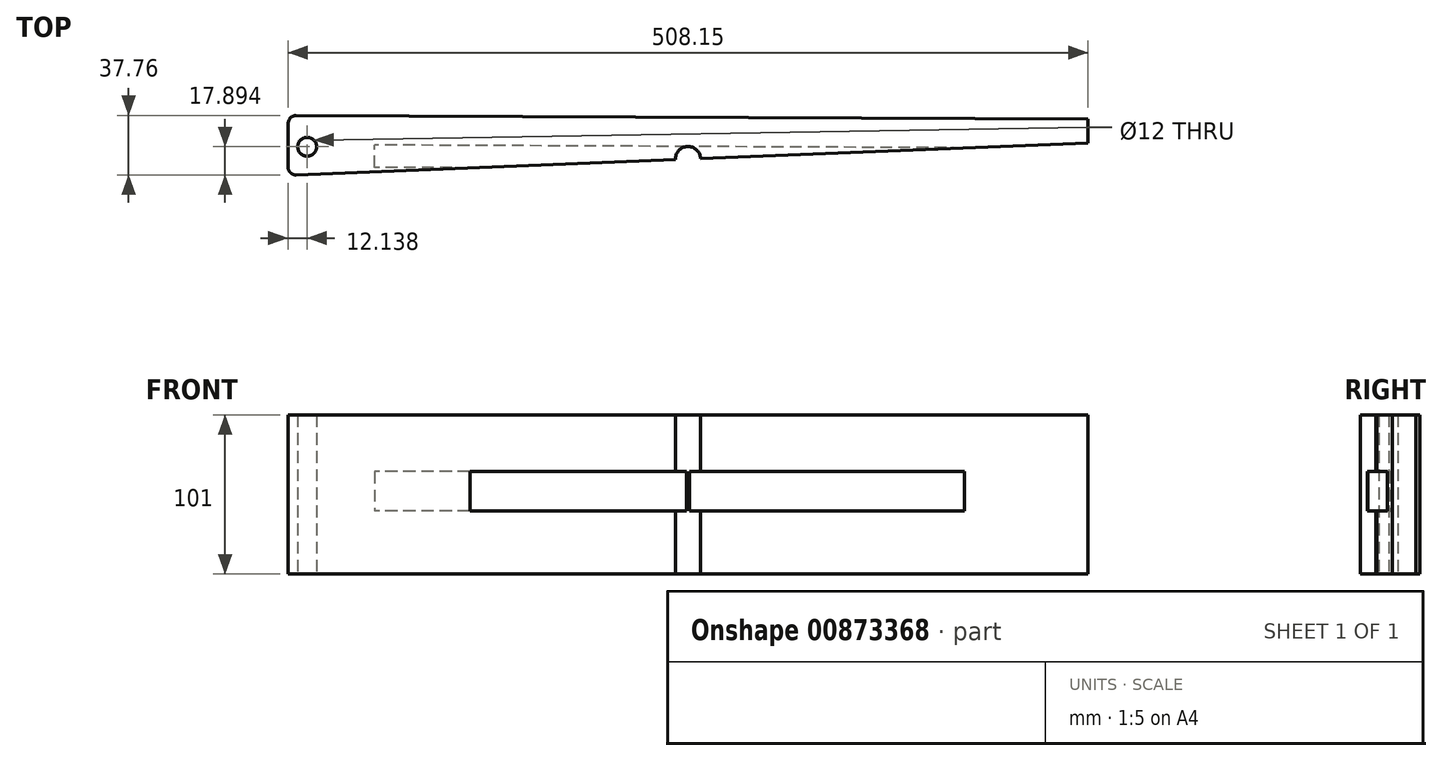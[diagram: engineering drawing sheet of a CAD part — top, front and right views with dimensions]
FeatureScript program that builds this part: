
annotation { "Feature Type Name" : "Feature", "Feature Type Description" : "" }
export const myFeature = defineFeature(function(context is Context, id is Id, definition is map)
    precondition{}
    {
        {
            var Q0;
            Q0=qCreatedBy(makeId("Top.planeOp"),FACE);
            var sketch = newSketch(context, id + "F0", { "sketchPlane" : qUnion([Q0])});
            skLineSegment(sketch, "E0.left", {"start": v(-253.96, 8.7) * mm, "end": v(-254.14, -29.3) * mm});
            skLineSegment(sketch, "E0.right", {"start": v(254.03, 6.3) * mm, "end": v(253.96, -8.7) * mm});
            skPoint(sketch, "E0.middle", {"position": v(0, 0) * mm});
            skLineSegment(sketch, "E1", {"start": v(-253.96, 8.7) * mm, "end": v(254.03, 6.3) * mm});
            skLineSegment(sketch, "E2", {"start": v(-254.14, -29.3) * mm, "end": v(253.96, -8.7) * mm});
            skCircle(sketch, "E3", {"center": v(-241.98, -11.19) * mm, "radius": 6 * mm});
            skPoint(sketch, "E3.centerSnap0", {"position": v(-254.14, -16.57) * mm});
            skCircle(sketch, "E4", {"center": v(-0.1, -19) * mm, "radius": 5 * mm});
            skCircle(sketch, "E5", {"center": v(-0.1, -19) * mm, "radius": 8 * mm});
            skLineSegment(sketch, "E6", {"start": v(-8.08, -19.32) * mm, "end": v(-5.09, -19.2) * mm});
            skLineSegment(sketch, "E7", {"start": v(4.9, -18.8) * mm, "end": v(7.9, -18.68) * mm});
            skSolve(sketch);
        }
        {
            var Q0;
            {var subQ1=sQuery(id+"F0.wireOp",EDGE,"E0.left");Q0=makeQuery(id+"F0.imprint","IMPRINT",FACE,{"disambiguationData":[TD([[makeQuery(id+"F0.imprint","IMPRINT",EDGE,{"derivedFrom":subQ1}),1.0]])]});}
            var Q1;
            {var subQ0=sQuery(id+"F0.wireOp",EDGE,"XZyqKKFk-1wkg-4Na5-50VD-DDx1DZDhWvUQ");Q1=makeQuery(id+"F0.imprint","IMPRINT",FACE,{"disambiguationData":[TD([[makeQuery(id+"F0.imprint","IMPRINT",EDGE,{"derivedFrom":subQ0}),1.0]])]});}
            var Q2;
            {var subQ5=sQuery(id+"F0.wireOp",EDGE,"XZyqKKFk-1wkg-4Na5-50VD-DDx1DZDhWvUQ");Q2=makeQuery(id+"F0.imprint","IMPRINT",FACE,{"disambiguationData":[TD([[makeQuery(id+"F0.imprint","IMPRINT",EDGE,{"derivedFrom":subQ5}),-1.0]])]});}
            var Q3;
            {var subQ5=sQuery(id+"F0.wireOp",EDGE,"MujNKNQA-XHeN-e8O0-YI1s-Rprdn2XYs7TK");Q3=makeQuery(id+"F0.imprint","IMPRINT",FACE,{"disambiguationData":[TD([[makeQuery(id+"F0.imprint","IMPRINT",EDGE,{"derivedFrom":subQ5}),1.0]])]});}
            var Q4;
            {var subQ0=sQuery(id+"F0.wireOp",EDGE,"E6");Q4=makeQuery(id+"F0.imprint","IMPRINT",FACE,{"disambiguationData":[TD([[makeQuery(id+"F0.imprint","IMPRINT",EDGE,{"derivedFrom":subQ0}),1.0]])]});}
            var Q5;
            {var subQ0=sQuery(id+"F0.wireOp",EDGE,"E6");Q5=makeQuery(id+"F0.imprint","IMPRINT",FACE,{"disambiguationData":[TD([[makeQuery(id+"F0.imprint","IMPRINT",EDGE,{"derivedFrom":subQ0}),-1.0]])]});}
            extrude(context, id + "F1", {"entities" : qUnion([Q0, Q1, Q2, Q3, Q4, Q5]), "depth" : 101 * mm, "offsetDistance" : 25 * mm});
        }
        {
            var Q0;
            Q0=makeQuery(id+"F1.opExtrude","SWEPT_EDGE",EDGE,{"disambiguationData":[OSD([sQuery(id+"F0.wireOp",EDGE,"E0.left"),sQuery(id+"F0.wireOp",EDGE,"E2")])]});
            var Q1;
            Q1=makeQuery(id+"F1.opExtrude","SWEPT_EDGE",EDGE,{"disambiguationData":[OSD([sQuery(id+"F0.wireOp",EDGE,"E0.left"),sQuery(id+"F0.wireOp",EDGE,"E1")])]});
            fillet(context, id + "F2", {"entities" : qUnion([Q0, Q1]), "radius" : 5 * mm, "tangentPropagation" : true, "allowEdgeOverflow" : false});
        }
        {
            var Q0;
            Q0=makeQuery(id+"F1.opExtrude","SWEPT_FACE",FACE,{"disambiguationData":[OSD([sQuery(id+"F0.wireOp",EDGE,"E0.left")])]});
            var sketch = newSketch(context, id + "F3", { "sketchPlane" : qUnion([Q0])});
            skLineSegment(sketch, "E8.0", {"start": v(19.35, 65) * mm, "end": v(19.35, 40) * mm});
            skLineSegment(sketch, "E9.0", {"start": v(30.26, 101) * mm, "end": v(30.26, 0) * mm});
            skLineSegment(sketch, "E10", {"start": v(19.35, 40) * mm, "end": v(30.26, 40) * mm});
            skLineSegment(sketch, "E11", {"start": v(30.26, 40) * mm, "end": v(30.26, 65) * mm});
            skLineSegment(sketch, "E12", {"start": v(30.26, 65) * mm, "end": v(19.35, 65) * mm});
            skLineSegment(sketch, "E13.0", {"start": v(11.05, 65) * mm, "end": v(19.35, 65) * mm});
            skLineSegment(sketch, "E14", {"start": v(11.05, 65) * mm, "end": v(11.05, 40) * mm});
            skLineSegment(sketch, "E15", {"start": v(11.05, 40) * mm, "end": v(19.35, 40) * mm});
            skSolve(sketch);
        }
        {
            var Q0;
            {var subQ0=sQuery(id+"F3.wireOp",EDGE,"E11");Q0=makeQuery(id+"F3.imprint","IMPRINT",FACE,{"disambiguationData":[TD([[makeQuery(id+"F3.imprint","IMPRINT",EDGE,{"derivedFrom":subQ0}),1.0]])]});}
            var Q1;
            {var subQ0=sQuery(id+"F3.wireOp",EDGE,"E8.0");Q1=makeQuery(id+"F3.imprint","IMPRINT",FACE,{"disambiguationData":[TD([[makeQuery(id+"F3.imprint","IMPRINT",EDGE,{"derivedFrom":subQ0}),1.0]])]});}
            var Q2;
            Q2=makeQuery(id+"F3.imprint","IMPRINT",FACE,{"disambiguationData":[TD([[makeQuery(id+"F3.imprint","IMPRINT",EDGE,{"derivedFrom":sQuery(id+"F3.wireOp",EDGE,"E8.0")}),-1.0]])]});
            var Q3;
            Q3=makeQuery(id+"F1.opExtrude","SWEPT_FACE",FACE,{"disambiguationData":[OSD([sQuery(id+"F0.wireOp",EDGE,"E0.right")])]});
            extrude(context, id + "F4", {"entities" : qUnion([Q0, Q1, Q2]), "operationType" : NewBodyOperationType.REMOVE, "endBound" : BoundingType.UP_TO_SURFACE, "oppositeDirection" : true, "depth" : 25 * mm, "endBoundEntityFace" : qUnion([Q3]), "offsetDistance" : 25 * mm, "hasSecondDirection" : true, "secondDirectionOppositeDirection" : true, "secondDirectionDepth" : 55 * mm});
        }
    });
